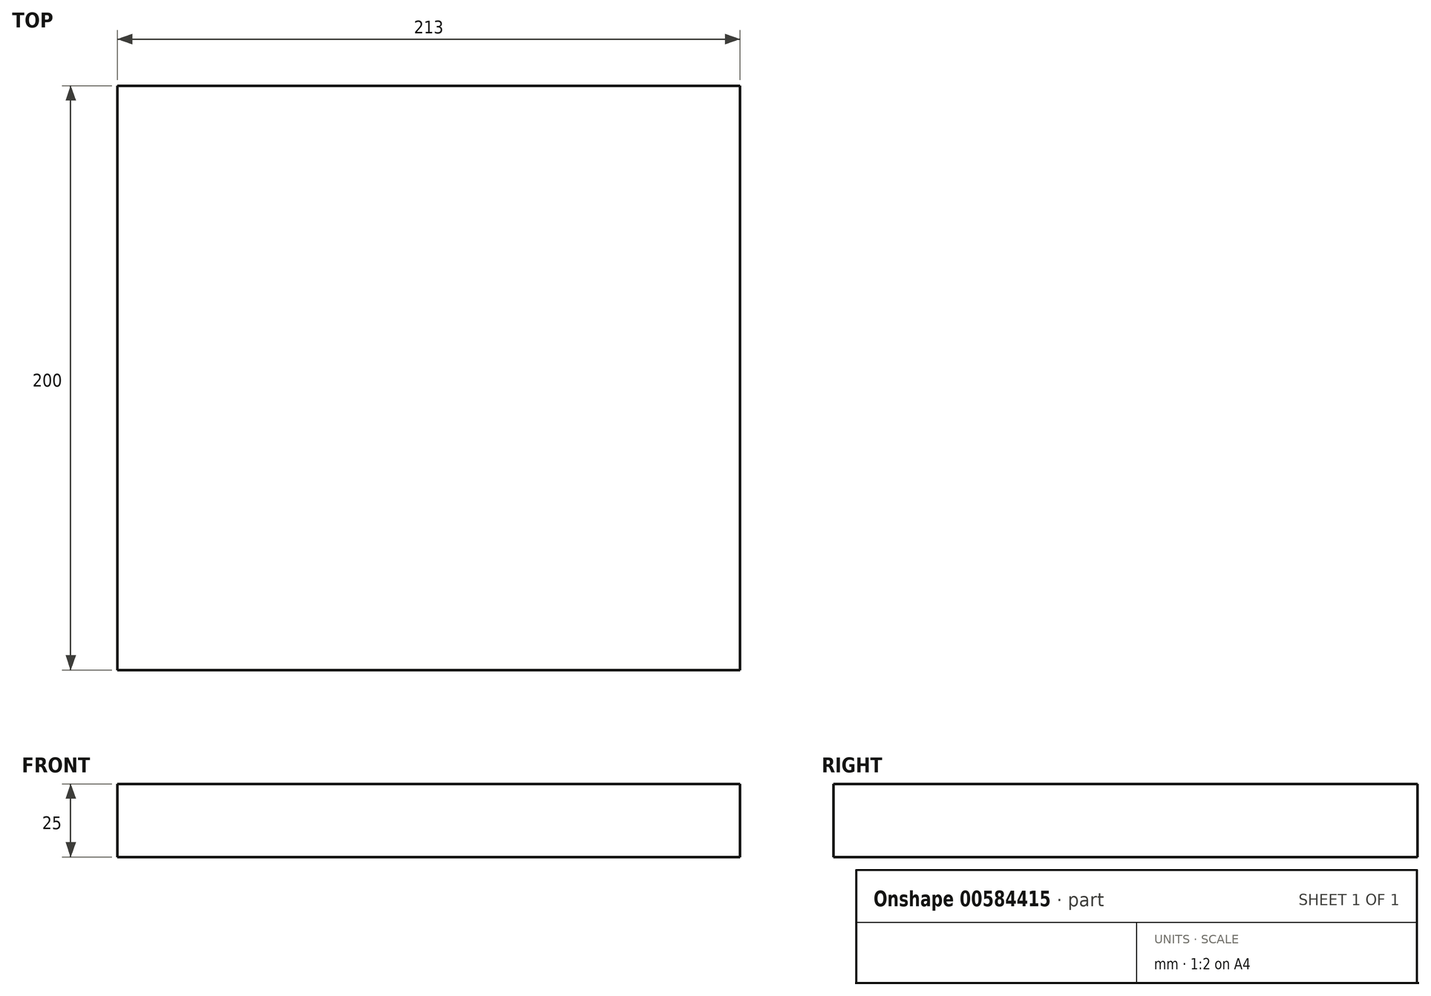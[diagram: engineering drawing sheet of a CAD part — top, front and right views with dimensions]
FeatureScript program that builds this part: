
annotation { "Feature Type Name" : "Feature", "Feature Type Description" : "" }
export const myFeature = defineFeature(function(context is Context, id is Id, definition is map)
    precondition{}
    {
        {
            var Q0;
            Q0=qCreatedBy(makeId("Top.planeOp"),FACE);
            var sketch = newSketch(context, id + "F0", { "sketchPlane" : qUnion([Q0])});
            skLineSegment(sketch, "E0.bottom", {"start": v(106.5, 100) * mm, "end": v(-106.5, 100) * mm});
            skLineSegment(sketch, "E0.top", {"start": v(106.5, -100) * mm, "end": v(-106.5, -100) * mm});
            skLineSegment(sketch, "E0.left", {"start": v(106.5, 100) * mm, "end": v(106.5, -100) * mm});
            skLineSegment(sketch, "E0.right", {"start": v(-106.5, 100) * mm, "end": v(-106.5, -100) * mm});
            skPoint(sketch, "E0.middle", {"position": v(0, 0) * mm});
            skSolve(sketch);
        }
        {
            var Q0;
            Q0=makeQuery(id+"F0.imprint","IMPRINT",FACE,{"disambiguationData":[TD([[makeQuery(id+"F0.imprint","IMPRINT",EDGE,{"derivedFrom":sQuery(id+"F0.wireOp",EDGE,"E0.bottom")}),1.0]])]});
            extrude(context, id + "F1", {"entities" : qUnion([Q0]), "depth" : 25 * mm, "offsetDistance" : 25 * mm});
        }
    });
